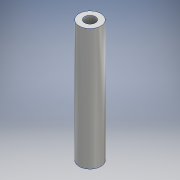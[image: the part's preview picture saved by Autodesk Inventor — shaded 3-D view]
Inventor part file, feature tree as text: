
AUTODESK INVENTOR PART (.ipt)
format: ipt  version: 2016 (Build 200138000, 138)  size: 105,984 bytes
history: native  units: mm
features: sketch x2, extrude x2, hole x2, other x1
ambient origin geometry x8: Origin, YZ Plane, XZ Plane, XY Plane, X Axis, Y Axis, Z Axis, Center Point
bodies: Body1 (feature_tree)
feature tree (7):
  other  "ソリッド1"
  sketch  "スケッチ1"
  extrude  "押し出し1"  Depth=8.0mm
  sketch  "スケッチ2"
  extrude  "押し出し2"  Depth=4.001mm
  hole  "穴1"  [1 undecoded]
  hole  "穴2"  [1 undecoded]
note: 2 required parameter values undecoded (feature->parameter linkage not recoverable at this tier; creation-order binding heuristic only, values carry confidence <= 0.55)
